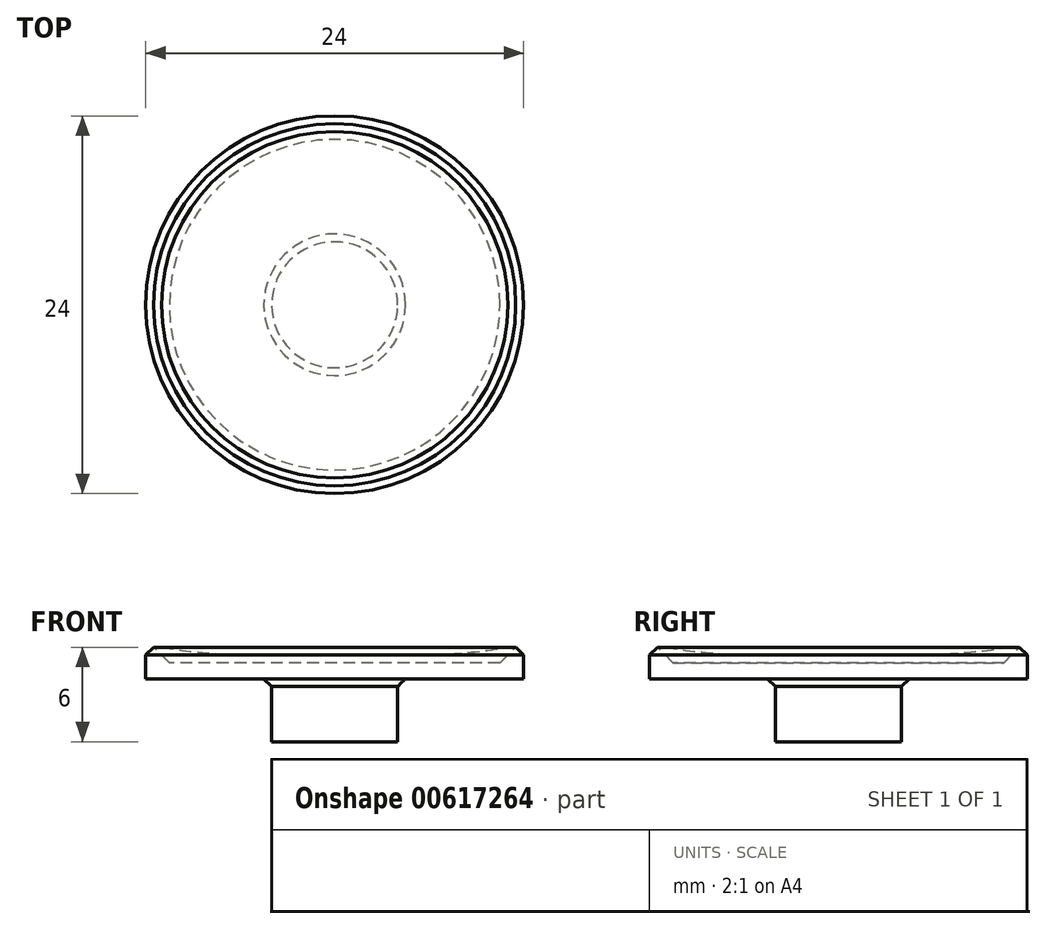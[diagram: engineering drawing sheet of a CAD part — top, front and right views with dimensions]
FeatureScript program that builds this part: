
annotation { "Feature Type Name" : "Feature", "Feature Type Description" : "" }
export const myFeature = defineFeature(function(context is Context, id is Id, definition is map)
    precondition{}
    {
        {
            var Q0;
            Q0=qCreatedBy(makeId("Front.planeOp"),FACE);
            var sketch = newSketch(context, id + "F0", { "sketchPlane" : qUnion([Q0])});
            skLineSegment(sketch, "E0", {"start": v(0, 0) * mm, "end": v(4, 0) * mm});
            skLineSegment(sketch, "E1", {"start": v(4, 0) * mm, "end": v(4, 3.5) * mm});
            skLineSegment(sketch, "E2", {"start": v(4, 3.5) * mm, "end": v(4.5, 4) * mm});
            skLineSegment(sketch, "E3", {"start": v(4.5, 4) * mm, "end": v(12, 4) * mm});
            skLineSegment(sketch, "E4", {"start": v(12, 4) * mm, "end": v(12, 6) * mm});
            skLineSegment(sketch, "E5", {"start": v(0, 5) * mm, "end": v(0, 0) * mm});
            skLineSegment(sketch, "E6", {"start": v(12, 6) * mm, "end": v(11.5, 6) * mm});
            skLineSegment(sketch, "E7", {"start": v(11.5, 6) * mm, "end": v(10.5, 5) * mm});
            skLineSegment(sketch, "E8", {"start": v(10.5, 5) * mm, "end": v(0, 5) * mm});
            skLineSegment(sketch, "E9", {"start": v(11.5, 6) * mm, "end": v(11, 6) * mm});
            skLineSegment(sketch, "E10", {"start": v(0, 5) * mm, "end": v(0, 5.5) * mm});
            skLineSegment(sketch, "E11", {"start": v(0, 5.5) * mm, "end": v(5, 5.5) * mm});
            skArc(sketch, "E12", {"start": v(5, 5.5) * mm, "mid": v(8.01, 5.63) * mm, "end": v(11, 6) * mm});
            skSolve(sketch);
        }
        {
            var Q0;
            Q0=makeQuery(id+"F0.imprint","IMPRINT",FACE,{"disambiguationData":[TD([[makeQuery(id+"F0.imprint","IMPRINT",EDGE,{"derivedFrom":sQuery(id+"F0.wireOp",EDGE,"E0")}),1.0]])]});
            var Q1;
            Q1=makeQuery(id+"F0.imprint","IMPRINT",FACE,{"disambiguationData":[TD([[makeQuery(id+"F0.imprint","IMPRINT",EDGE,{"derivedFrom":sQuery(id+"F0.wireOp",EDGE,"8oDHqX6i-wsKN-9OYi-xL7f-mJhccouFAabg")}),1.0]])]});
            var Q2;
            Q2=sQuery(id+"F0.wireOp",EDGE,"E5");
            revolve(context, id + "F1", {"entities" : qUnion([Q0, Q1]), "axis" : qUnion([Q2]), "revolveType" : RevolveType.FULL});
        }
        {
            var Q0;
            Q0=makeQuery(id+"F0.imprint","IMPRINT",FACE,{"disambiguationData":[TD([[makeQuery(id+"F0.imprint","IMPRINT",EDGE,{"derivedFrom":sQuery(id+"F0.wireOp",EDGE,"E7")}),-1.0]])]});
            var Q1;
            Q1=sQuery(id+"F0.wireOp",EDGE,"E5");
            revolve(context, id + "F2", {"entities" : qUnion([Q0]), "axis" : qUnion([Q1]), "revolveType" : RevolveType.FULL});
        }
        {
            var Q0;
            Q0=makeQuery(id+"F1.opRevolve","SWEPT_EDGE",EDGE,{"disambiguationData":[OSD([sQuery(id+"F0.wireOp",EDGE,"E4"),sQuery(id+"F0.wireOp",EDGE,"E6")])]});
            chamfer(context, id + "F3", {"entities" : qUnion([Q0]), "width" : 0.5 * mm, "tangentPropagation" : true});
        }
    });
